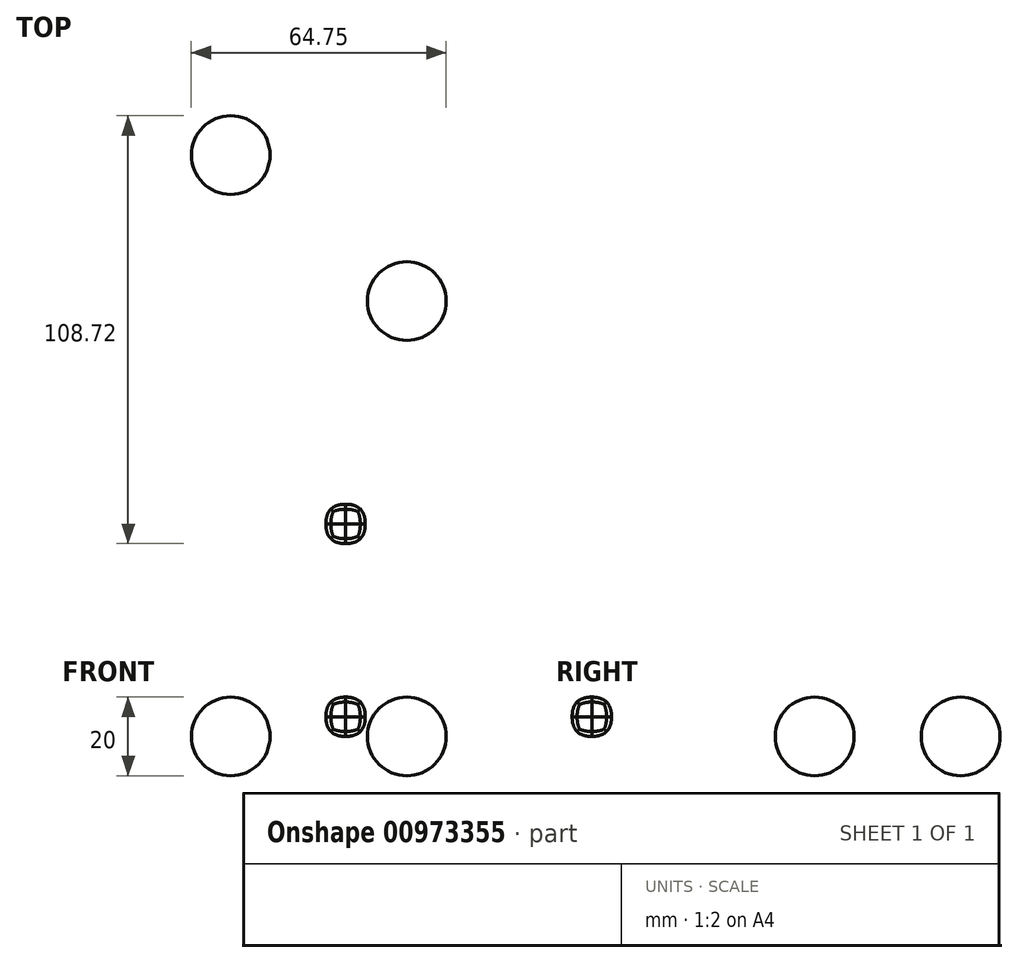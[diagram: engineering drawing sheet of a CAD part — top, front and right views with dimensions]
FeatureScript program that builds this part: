
annotation { "Feature Type Name" : "Feature", "Feature Type Description" : "" }
export const myFeature = defineFeature(function(context is Context, id is Id, definition is map)
    precondition{}
    {
        {
            var Q0;
            Q0=qCreatedBy(makeId("Top.planeOp"),FACE);
            var sketch = newSketch(context, id + "F0", { "sketchPlane" : qUnion([Q0])});
            skCircle(sketch, "E0", {"center": v(0, 0) * mm, "radius": 10 * mm});
            skSolve(sketch);
        }
        {
            var Q0;
            Q0=makeQuery(id+"F0.imprint","IMPRINT",FACE,{"disambiguationData":[TD([[makeQuery(id+"F0.imprint","IMPRINT",EDGE,{"derivedFrom":sQuery(id+"F0.wireOp",EDGE,"E0")}),1.0]])]});
            extrude(context, id + "F1", {"entities" : qUnion([Q0]), "depth" : 20 * mm, "offsetDistance" : 25 * mm, "symmetric" : true});
        }
        {
            var Q0;
            Q0=makeQuery(id+"F1.opExtrude","CAP_EDGE",EDGE,{"disambiguationData":[OSD([sQuery(id+"F0.wireOp",EDGE,"E0")])],"isStart":true});
            var Q1;
            Q1=makeQuery(id+"F1.opExtrude","CAP_EDGE",EDGE,{"disambiguationData":[OSD([sQuery(id+"F0.wireOp",EDGE,"E0")])],"isStart":false});
            fillet(context, id + "F2", {"entities" : qUnion([Q0, Q1]), "tangentPropagation" : true, "radius" : 10 * mm, "defaultsChanged" : true, "vertexSettings" : [], "allowEdgeOverflow" : false});
        }
        {
            var Q0;
            Q0=qCreatedBy(makeId("Top.planeOp"),FACE);
            var sketch = newSketch(context, id + "F3", { "sketchPlane" : qUnion([Q0])});
            skArc(sketch, "E1", {"start": v(-44.75, 27.1) * mm, "mid": v(-34.75, 37.1) * mm, "end": v(-44.75, 47.1) * mm});
            skLineSegment(sketch, "E2", {"start": v(-44.75, 47.1) * mm, "end": v(-44.75, 27.1) * mm});
            skSolve(sketch);
        }
        {
            var Q0;
            Q0 = qSketchRegion(id + "F3", true);
            var Q1;
            Q1=sQuery(id+"F3.wireOp",EDGE,"E2");
            revolve(context, id + "F4", {"surfaceOperationType" : NewSurfaceOperationType.NEW, "entities" : qUnion([Q0]), "axis" : qUnion([Q1]), "revolveType" : RevolveType.FULL});
        }
        {
            var Q0;
            Q0=qCreatedBy(makeId("Top.planeOp"),FACE);
            var sketch = newSketch(context, id + "F5", { "sketchPlane" : qUnion([Q0])});
            skLineSegment(sketch, "E3.bottom", {"start": v(-20.56, -51.61) * mm, "end": v(-10.56, -51.61) * mm});
            skLineSegment(sketch, "E3.top", {"start": v(-20.56, -61.61) * mm, "end": v(-10.56, -61.61) * mm});
            skLineSegment(sketch, "E3.left", {"start": v(-20.56, -51.61) * mm, "end": v(-20.56, -61.61) * mm});
            skLineSegment(sketch, "E3.right", {"start": v(-10.56, -51.61) * mm, "end": v(-10.56, -61.61) * mm});
            skPoint(sketch, "E3.middle", {"position": v(-15.56, -56.61) * mm});
            skSolve(sketch);
        }
        {
            var Q0;
            Q0 = qSketchRegion(id + "F5", true);
            extrude(context, id + "F6", {"entities" : qUnion([Q0]), "depth" : 10 * mm, "offsetDistance" : 25 * mm});
        }
        {
            var Q0;
            Q0=makeQuery(id+"F6.opExtrude","CAP_FACE",FACE,{"disambiguationData":[OSD([sQuery(id+"F5.wireOp",EDGE,"E3.bottom"),sQuery(id+"F5.wireOp",EDGE,"E3.top"),sQuery(id+"F5.wireOp",EDGE,"E3.left"),sQuery(id+"F5.wireOp",EDGE,"E3.right")])],"isStart":false});
            var Q1;
            Q1=makeQuery(id+"F6.opExtrude","SWEPT_FACE",FACE,{"disambiguationData":[OSD([sQuery(id+"F5.wireOp",EDGE,"E3.top")])]});
            var Q2;
            Q2=makeQuery(id+"F6.opExtrude","SWEPT_FACE",FACE,{"disambiguationData":[OSD([sQuery(id+"F5.wireOp",EDGE,"E3.left")])]});
            var Q3;
            Q3=makeQuery(id+"F6.opExtrude","SWEPT_FACE",FACE,{"disambiguationData":[OSD([sQuery(id+"F5.wireOp",EDGE,"E3.right")])]});
            var Q4;
            Q4=makeQuery(id+"F6.opExtrude","SWEPT_FACE",FACE,{"disambiguationData":[OSD([sQuery(id+"F5.wireOp",EDGE,"E3.bottom")])]});
            var Q5;
            Q5=makeQuery(id+"F6.opExtrude","CAP_FACE",FACE,{"disambiguationData":[OSD([sQuery(id+"F5.wireOp",EDGE,"E3.bottom"),sQuery(id+"F5.wireOp",EDGE,"E3.top"),sQuery(id+"F5.wireOp",EDGE,"E3.left"),sQuery(id+"F5.wireOp",EDGE,"E3.right")])],"isStart":true});
            fillet(context, id + "F7", {"entities" : qUnion([Q0, Q1, Q2, Q3, Q4, Q5]), "tangentPropagation" : true, "crossSection" : FilletCrossSection.CONIC, "radius" : 5 * mm, "rho" : 0.5, "defaultsChanged" : false, "vertexSettings" : [], "allowEdgeOverflow" : false});
        }
    });
